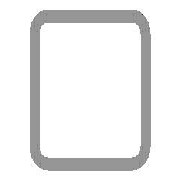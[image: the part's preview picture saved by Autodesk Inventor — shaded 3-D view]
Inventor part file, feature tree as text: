
AUTODESK INVENTOR PART (.ipt)
format: ipt  version: 2025 (Build 290162010, 162A)  size: 134,656 bytes
history: native  units: mm (DEFAULTED — no unit token found)
features: other x4, sketch x1, plane x1
ambient origin geometry x8: Origin, YZ Plane, XZ Plane, XY Plane, X Axis, Y Axis, Z Axis, Center Point
bodies: Solid1 (feature_tree), Body (feature_tree)
feature tree (6):
  parser-record x1  (decoder bookkeeping rows leaked as tree rows — omitted from the tree; the rows remain in map.json)
  other  "Driven Length"
  other  "Start Plane"
  other  "End Plane"
  sketch  "Sketch3"  dims[d3=1210.0mm d4=0.0mm d7=4.0mm d9=40.0mm d11=40.0mm d12=2.0mm d13=-0.0mm d14=1210.0mm d15=20.0mm d16=20.0mm d17=90.0deg d18=1210.0mm]
  plane  "Work Plane3"
